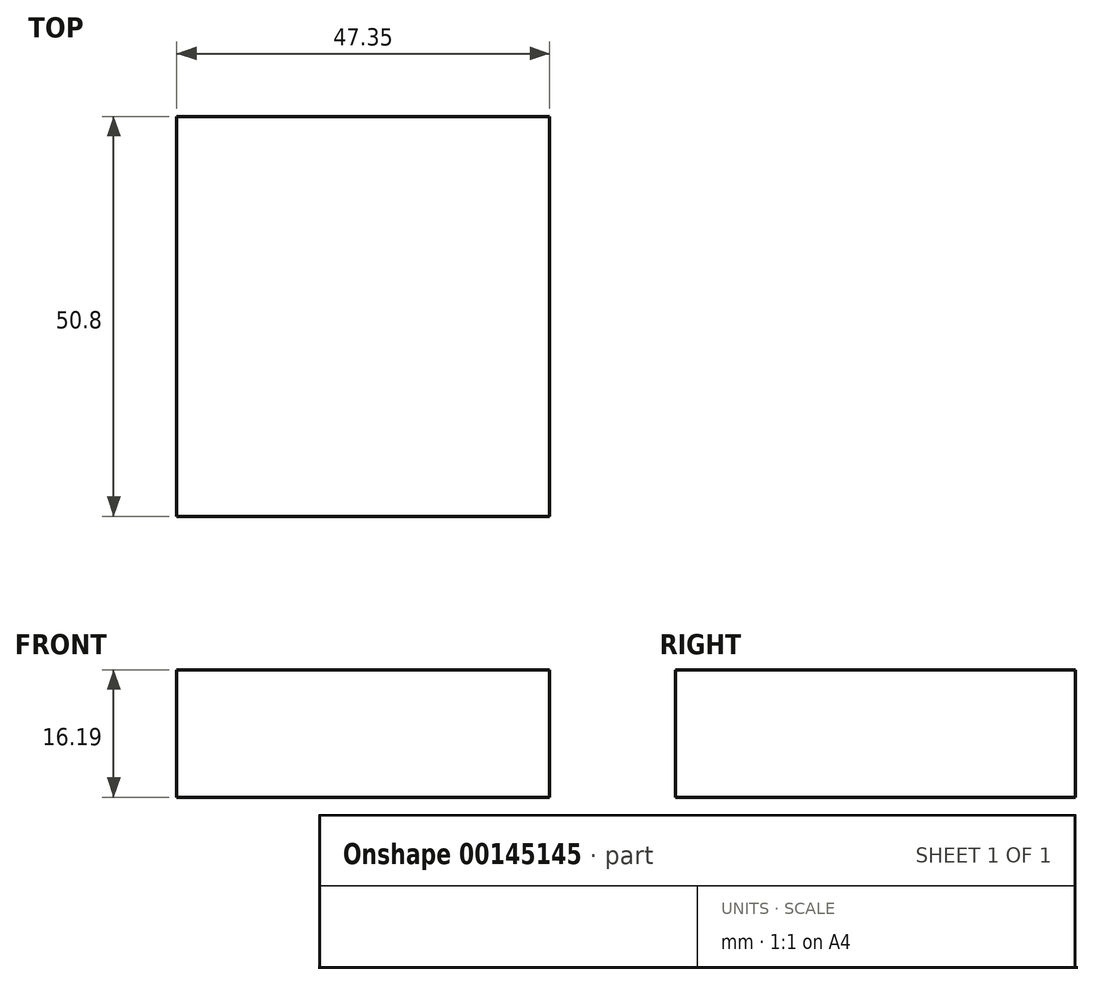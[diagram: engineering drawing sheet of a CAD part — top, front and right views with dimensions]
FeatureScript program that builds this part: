
annotation { "Feature Type Name" : "Feature", "Feature Type Description" : "" }
export const myFeature = defineFeature(function(context is Context, id is Id, definition is map)
    precondition{}
    {
        {
            var Q0;
            Q0=qCreatedBy(makeId("Front.planeOp"),FACE);
            var sketch = newSketch(context, id + "F0", { "sketchPlane" : qUnion([Q0])});
            skLineSegment(sketch, "E0.bottom", {"start": v(-58.44, 40.5) * mm, "end": v(48.2, 40.5) * mm});
            skLineSegment(sketch, "E0.top", {"start": v(-58.44, -37.49) * mm, "end": v(48.2, -37.49) * mm});
            skLineSegment(sketch, "E0.left", {"start": v(-58.44, 40.5) * mm, "end": v(-58.44, -37.49) * mm});
            skLineSegment(sketch, "E0.right", {"start": v(48.2, 40.5) * mm, "end": v(48.2, -37.49) * mm});
            skLineSegment(sketch, "E1.bottom", {"start": v(52.47, -35.83) * mm, "end": v(99.82, -35.83) * mm});
            skLineSegment(sketch, "E1.top", {"start": v(52.47, -52.02) * mm, "end": v(99.82, -52.02) * mm});
            skLineSegment(sketch, "E1.left", {"start": v(52.47, -35.83) * mm, "end": v(52.47, -52.02) * mm});
            skLineSegment(sketch, "E1.right", {"start": v(99.82, -35.83) * mm, "end": v(99.82, -52.02) * mm});
            skSolve(sketch);
        }
        {
            var Q0;
            Q0=makeQuery(id+"F0.imprint","IMPRINT",FACE,{"disambiguationData":[TD([[makeQuery(id+"F0.imprint","IMPRINT",EDGE,{"derivedFrom":sQuery(id+"F0.wireOp",EDGE,"E1.bottom")}),-1.0]])]});
            extrude(context, id + "F1", {"entities" : qUnion([Q0]), "depth" : 50.8 * mm});
        }
    });
